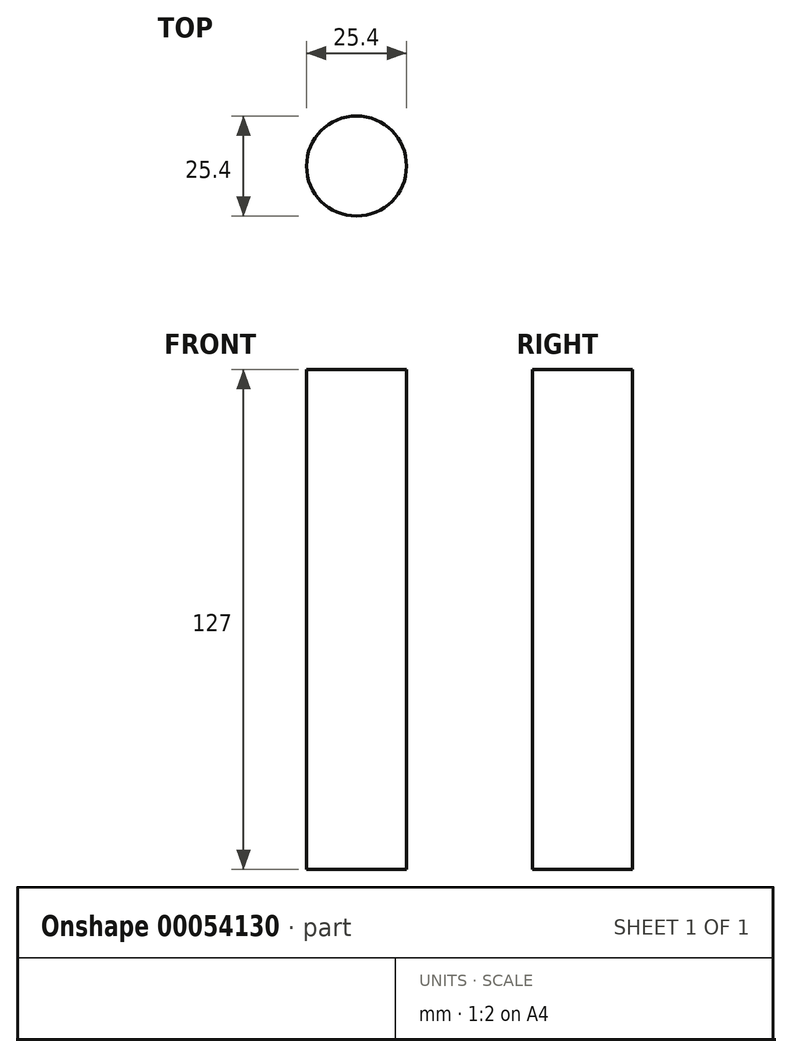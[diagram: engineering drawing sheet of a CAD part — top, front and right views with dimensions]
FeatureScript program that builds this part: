
annotation { "Feature Type Name" : "Feature", "Feature Type Description" : "" }
export const myFeature = defineFeature(function(context is Context, id is Id, definition is map)
    precondition{}
    {
        {
            var Q0;
            Q0=qCreatedBy(makeId("Top.planeOp"),FACE);
            var sketch = newSketch(context, id + "F0", { "sketchPlane" : qUnion([Q0])});
            skCircle(sketch, "E0", {"center": v(0, 0) * mm, "radius": 12.7 * mm});
            skSolve(sketch);
        }
        {
            var Q0;
            Q0 = qSketchRegion(id + "F0", true);
            extrude(context, id + "F1", {"entities" : qUnion([Q0]), "depth" : 127 * mm});
        }
    });
